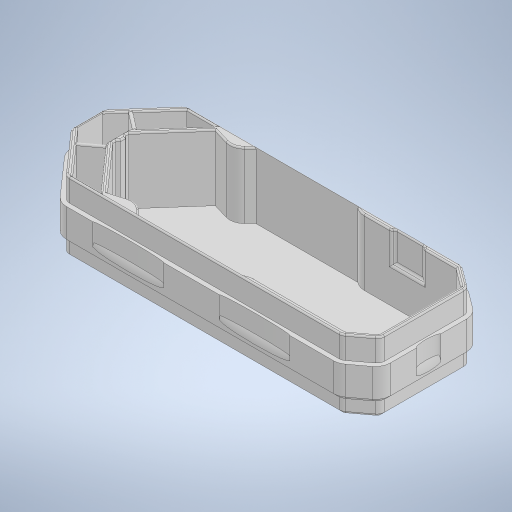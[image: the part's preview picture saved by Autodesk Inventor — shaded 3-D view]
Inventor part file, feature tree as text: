
AUTODESK INVENTOR PART (.ipt)
format: ipt  version: 2024.1 (Build 281209000, 209)  size: 1,627,648 bytes
history: native  units: mm
features: extrude x18, sketch x18, projected_geometry x18, fillet x14, chamfer x4, other x2, plane x2, mirror x1, pattern_circular x1
ambient origin geometry x8: Origin, YZ Plane, XZ Plane, XY Plane, X Axis, Y Axis, Z Axis, Center Point
bodies: Solid1 (feature_tree), Solid2 (feature_tree)
feature tree (78):
  extrude  "44mm-body"  Depth=3.0mm TaperAngle=0.0deg
  extrude  "Extrusion2"  Depth=3.0mm
  extrude  "Extrusion3"  Depth=3.0mm
  extrude  "Extrusion8"  Depth=32.0mm TaperAngle=0.0deg
  extrude  "Extrusion10"  Depth=4.0mm TaperAngle=0.0deg
  extrude  "Extrusion4"  Depth=10.0mm
  extrude  "Extrusion11"  Depth=10.0mm
  extrude  "Extrusion5"  Depth=10.0mm
  extrude  "Extrusion6"  Depth=4.0mm TaperAngle=45.0deg
  fillet  "Fillet1"  Radius=3.0mm
  fillet  "Fillet2"  Radius=3.0mm
  fillet  "Fillet3"  Radius=12.4mm
  fillet  "Fillet4"  Radius=55.0mm
  extrude  "Extrusion7"  Depth=9.25mm
  fillet  "Fillet5"  Radius=3.4mm
  other  "Work Axis1"
  mirror  "Mirror1"
  pattern_circular  "Circular Pattern1"  [2 undecoded]
  chamfer  "Chamfer1"  Distance=8.0mm
  chamfer  "Chamfer2"  Distance=8.0mm
  extrude  "Extrusion12"  Depth=0.4mm
  extrude  "Extrusion13"  Depth=0.4mm
  extrude  "Extrusion14"  Depth=0.4mm
  extrude  "Extrusion15"  Depth=0.4mm
  extrude  "Extrusion16"  Depth=0.4mm
  fillet  "Fillet6"  Radius=1.5mm
  extrude  "Extrusion17"  Depth=0.4mm
  extrude  "Extrusion18"  Depth=0.4mm
  fillet  "Fillet7"  Radius=14.3mm
  fillet  "Fillet8"  Radius=49.0mm
  extrude  "Extrusion19"  Depth=0.4mm
  fillet  "Fillet14"  Radius=49.0mm
  chamfer  "Chamfer3"  Distance=3.0mm
  fillet  "Fillet9"  Radius=3.0mm
  chamfer  "Chamfer4"  Distance=2.5mm
  fillet  "Fillet11"  Radius=22.0mm
  fillet  "Fillet10"  Radius=2.0mm
  fillet  "Fillet12"  Radius=1.5mm
  fillet  "Fillet13"  Radius=14.2mm
  sketch  "Sketch1"  dims[d4=44.0mm d5=0.0mm d6=3.0mm d7=0.0mm]
  sketch  "Sketch2"  dims[d44=3.0mm d45=3.0mm]
  projected_geometry  "Projected Loop1"
  sketch  "Sketch3"  dims[d46=3.0mm d47=3.0mm]
  projected_geometry  "Projected Loop2"
  sketch  "Sketch4"  dims[d48=0.0mm d49=0.0mm d53=32.0mm d54=0.0mm]
  projected_geometry  "Projected Loop3"
  sketch  "Sketch5"  dims[d55=16.0mm d56=0.0mm d57=4.0mm d58=0.0mm]
  projected_geometry  "Projected Loop4"
  sketch  "Sketch6"  dims[d59=5.0mm d60=10.0mm]
  projected_geometry  "Projected Loop5"
  sketch  "Sketch7"  dims[d61=10.0mm d62=10.0mm]
  plane  "Work Plane1"
  plane  "Work Plane2"
  sketch  "Sketch8"  dims[d63=12.0mm d64=0.0mm d65=10.0mm]
  sketch  "Sketch11"  dims[d66=20.0mm d67=360.0deg d69=4.0mm d70=2.0mm d71=45.0deg]
  sketch  "Sketch13"  dims[d72=4.0mm d73=2.0mm d74=45.0deg d75=3.0mm d76=3.0mm d77=12.4mm d78=55.0mm]
  projected_geometry  "Projected Loop6"
  sketch  "Sketch14"  dims[d79=9.25mm d80=9.25mm d81=3.4mm]
  sketch  "Sketch15"  dims[d82=3.4mm]
  projected_geometry  "Projected Loop7"
  sketch  "Sketch16"  dims[d83=80.4mm]
  projected_geometry  "Projected Loop8"
  projected_geometry  "Projected Loop9"
  projected_geometry  "Projected Loop10"
  projected_geometry  "Projected Loop11"
  other  "battery"
  sketch  "Sketch17"  dims[d84=136.0mm]
  projected_geometry  "Projected Loop12"
  projected_geometry  "Projected Loop13"
  projected_geometry  "Projected Loop14"
  projected_geometry  "Projected Loop15"
  sketch  "Sketch18"  dims[d85=2.5mm]
  projected_geometry  "Projected Loop16"
  projected_geometry  "Projected Loop17"
  sketch  "Sketch19"  dims[d87=2.5mm]
  sketch  "Sketch20"  dims[d88=8.0mm]
  sketch  "Sketch22"  dims[d89=14.0mm d90=198.0mm d91=8.0mm d92=8.0mm d93=16.0mm d94=72.0mm d95=80.3mm d96=33.15mm d97=4.15mm d98=1.5mm d99=2.0mm d100=2.0mm d101=14.3mm d102=49.0mm d103=14.3mm d104=49.0mm d105=3.0mm d106=3.0mm d107=2.5mm d108=22.0mm d109=0.0mm d121=2.0mm d122=1.5mm d123=14.2mm d124=3.1mm d125=2.0mm d126=14.2mm d127=18.25mm d128=0.0mm d129=3.0mm d130=3.0mm d131=3.0mm d132=3.0mm d133=3.0mm d134=32.0mm d135=0.0mm d136=0.1mm d137=0.0mm d138=14.2mm d139=2.0mm d140=0.0mm d141=50.2mm d142=0.0mm d143=16.0mm d144=3.0mm d145=0.0mm d146=6.5mm d147=0.5mm d148=0.0mm d149=2.0mm d153=2.0mm d154=2.0mm d155=0.5mm d156=0.0mm d157=23.0mm d158=20.0mm d159=1.5mm d160=20.0mm d161=0.0mm d162=2.0mm d163=1.0mm d164=1.0mm d165=10.0mm d166=0.0mm d167=2.5mm d168=2.0mm d169=45.0deg d170=3.0mm d171=2.0mm d172=45.0deg d173=1.736086mm d174=67.0mm d175=47.137037mm d176=43.431481mm d177=1.321163mm d178=23.568519mm d179=8.479885mm d180=8.0mm d181=1.0mm d182=10.0mm d183=0.9mm d184=0.4mm d185=5.0mm]
  projected_geometry  "Projected Loop18"
note: 2 required parameter values undecoded (feature->parameter linkage not recoverable at this tier; creation-order binding heuristic only, values carry confidence <= 0.55)
